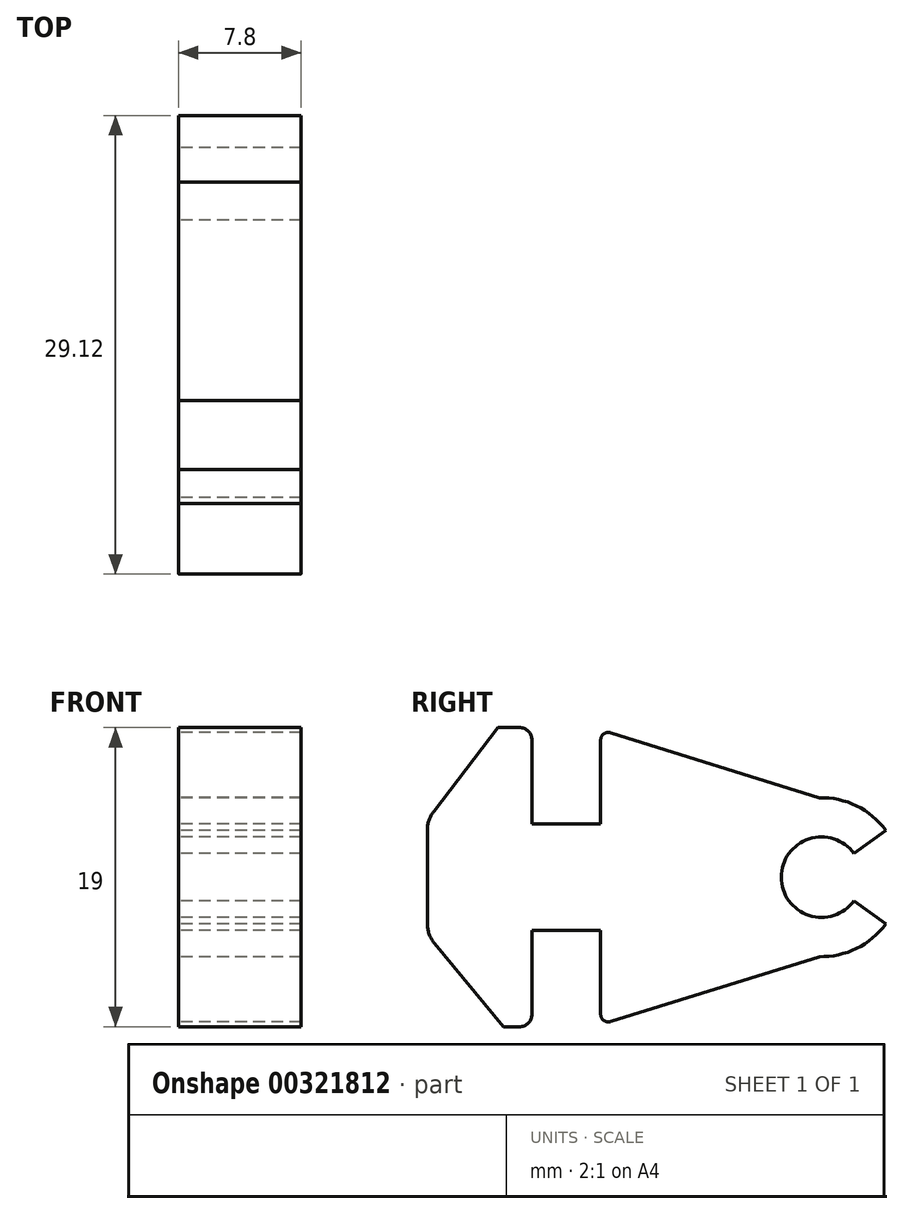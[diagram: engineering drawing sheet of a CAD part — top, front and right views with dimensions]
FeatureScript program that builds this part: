
annotation { "Feature Type Name" : "Feature", "Feature Type Description" : "" }
export const myFeature = defineFeature(function(context is Context, id is Id, definition is map)
    precondition{}
    {
        {
            var Q0;
            Q0=qCreatedBy(makeId("Right.planeOp"),FACE);
            var sketch = newSketch(context, id + "F0", { "sketchPlane" : qUnion([Q0])});
            skLineSegment(sketch, "E0", {"start": v(-2.33, 1.82) * mm, "end": v(-6.7, 1.82) * mm});
            skLineSegment(sketch, "E1", {"start": v(-6.7, 1.82) * mm, "end": v(-6.7, 7.15) * mm});
            skLineSegment(sketch, "E2", {"start": v(-7.5, 7.95) * mm, "end": v(-8.86, 7.95) * mm});
            skLineSegment(sketch, "E3", {"start": v(-8.86, 7.95) * mm, "end": v(-12.92, 2.63) * mm});
            skLineSegment(sketch, "E4", {"start": v(-13.34, 1.42) * mm, "end": v(-13.34, -4.48) * mm});
            skLineSegment(sketch, "E5", {"start": v(-12.88, -5.76) * mm, "end": v(-8.5, -11.05) * mm});
            skLineSegment(sketch, "E6", {"start": v(-8.5, -11.05) * mm, "end": v(-7.5, -11.05) * mm});
            skLineSegment(sketch, "E7", {"start": v(-6.7, -10.25) * mm, "end": v(-6.7, -4.93) * mm});
            skLineSegment(sketch, "E8", {"start": v(-6.7, -4.93) * mm, "end": v(-2.33, -4.93) * mm});
            skLineSegment(sketch, "E9", {"start": v(-2.33, -4.93) * mm, "end": v(-2.33, -10.93) * mm});
            skLineSegment(sketch, "E10", {"start": v(-2.33, -10.93) * mm, "end": v(11.56, -6.6) * mm});
            skLineSegment(sketch, "E11", {"start": v(11.55, 3.5) * mm, "end": v(-2.33, 7.82) * mm});
            skLineSegment(sketch, "E12", {"start": v(-2.33, 7.82) * mm, "end": v(-2.33, 1.82) * mm});
            skLineSegment(sketch, "E13", {"start": v(-6.7, 1.82) * mm, "end": v(-6.7, -4.93) * mm, "construction": true});
            skLineSegment(sketch, "E14", {"start": v(-6.7, -1.55) * mm, "end": v(-13.34, -1.55) * mm, "construction": true});
            skPoint(sketch, "E15.visualSharp", {"position": v(-6.7, -11.05) * mm});
            skArc(sketch, "E15.filletArc", {"start": v(-7.5, -11.05) * mm, "mid": v(-6.92, -10.82) * mm, "end": v(-6.7, -10.25) * mm});
            skPoint(sketch, "E16.visualSharp", {"position": v(-6.7, 7.95) * mm});
            skArc(sketch, "E16.filletArc", {"start": v(-6.7, 7.15) * mm, "mid": v(-6.92, 7.71) * mm, "end": v(-7.5, 7.95) * mm});
            skPoint(sketch, "E17.visualSharp", {"position": v(-13.34, 2.1) * mm});
            skArc(sketch, "E17.filletArc", {"start": v(-12.92, 2.63) * mm, "mid": v(-13.23, 2.06) * mm, "end": v(-13.34, 1.42) * mm});
            skPoint(sketch, "E18.visualSharp", {"position": v(-13.34, -5.2) * mm});
            skArc(sketch, "E18.filletArc", {"start": v(-13.34, -4.48) * mm, "mid": v(-13.22, -5.16) * mm, "end": v(-12.88, -5.76) * mm});
            skLineSegment(sketch, "E19", {"start": v(9.14, -1.55) * mm, "end": v(-6.7, -1.55) * mm, "construction": true});
            skCircle(sketch, "E20", {"center": v(11.7, -1.55) * mm, "radius": 2.55 * mm});
            skArc(sketch, "E21.0", {"start": v(11.56, -6.6) * mm, "mid": v(16.74, -1.55) * mm, "end": v(11.55, 3.5) * mm});
            skPoint(sketch, "E22.orphan", {"position": v(11.7, 3.45) * mm});
            skPoint(sketch, "E23.orphan", {"position": v(11.7, -6.56) * mm});
            skSolve(sketch);
        }
        {
            var Q0;
            Q0=makeQuery(id+"F0.imprint","IMPRINT",FACE,{"disambiguationData":[TD([[makeQuery(id+"F0.imprint","IMPRINT",EDGE,{"derivedFrom":sQuery(id+"F0.wireOp",EDGE,"E0")}),1.0]])]});
            extrude(context, id + "F1", {"entities" : qUnion([Q0]), "depth" : 7.8 * mm});
        }
        {
            var Q0;
            Q0=makeQuery(id+"F1.opExtrude","SWEPT_EDGE",EDGE,{"disambiguationData":[OSD([sQuery(id+"F0.wireOp",EDGE,"E11"),sQuery(id+"F0.wireOp",EDGE,"E12")])]});
            var Q1;
            Q1=makeQuery(id+"F1.opExtrude","SWEPT_EDGE",EDGE,{"disambiguationData":[OSD([sQuery(id+"F0.wireOp",EDGE,"E9"),sQuery(id+"F0.wireOp",EDGE,"E10")])]});
            fillet(context, id + "F2", {"entities" : qUnion([Q0, Q1]), "radius" : .5 * mm, "tangentPropagation" : true, "allowEdgeOverflow" : false});
        }
        {
            var Q0;
            Q0=makeQuery(id+"F1.opExtrude","CAP_FACE",FACE,{"disambiguationData":[OSD([sQuery(id+"F0.wireOp",EDGE,"E0"),sQuery(id+"F0.wireOp",EDGE,"E1"),sQuery(id+"F0.wireOp",EDGE,"E2"),sQuery(id+"F0.wireOp",EDGE,"E3"),sQuery(id+"F0.wireOp",EDGE,"E4"),sQuery(id+"F0.wireOp",EDGE,"E5"),sQuery(id+"F0.wireOp",EDGE,"E6"),sQuery(id+"F0.wireOp",EDGE,"E7"),sQuery(id+"F0.wireOp",EDGE,"E8"),sQuery(id+"F0.wireOp",EDGE,"E9"),sQuery(id+"F0.wireOp",EDGE,"E10"),sQuery(id+"F0.wireOp",EDGE,"E11"),sQuery(id+"F0.wireOp",EDGE,"E12"),sQuery(id+"F0.wireOp",EDGE,"E15.filletArc"),sQuery(id+"F0.wireOp",EDGE,"E16.filletArc"),sQuery(id+"F0.wireOp",EDGE,"E17.filletArc"),sQuery(id+"F0.wireOp",EDGE,"E18.filletArc"),sQuery(id+"F0.wireOp",EDGE,"E20"),sQuery(id+"F0.wireOp",EDGE,"E21.0")])],"isStart":false});
            var sketch = newSketch(context, id + "F3", { "sketchPlane" : qUnion([Q0])});
            skLineSegment(sketch, "E24", {"start": v(11.7, -1.55) * mm, "end": v(19.31, 3.98) * mm});
            skLineSegment(sketch, "E25", {"start": v(19.31, 3.98) * mm, "end": v(19.31, -7.09) * mm});
            skLineSegment(sketch, "E26", {"start": v(19.31, -7.09) * mm, "end": v(11.7, -1.55) * mm});
            skSolve(sketch);
        }
        {
            var Q0;
            Q0 = qSketchRegion(id + "F3", true);
            extrude(context, id + "F4", {"entities" : qUnion([Q0]), "operationType" : NewBodyOperationType.REMOVE, "oppositeDirection" : true, "depth" : 25 * mm});
        }
    });
